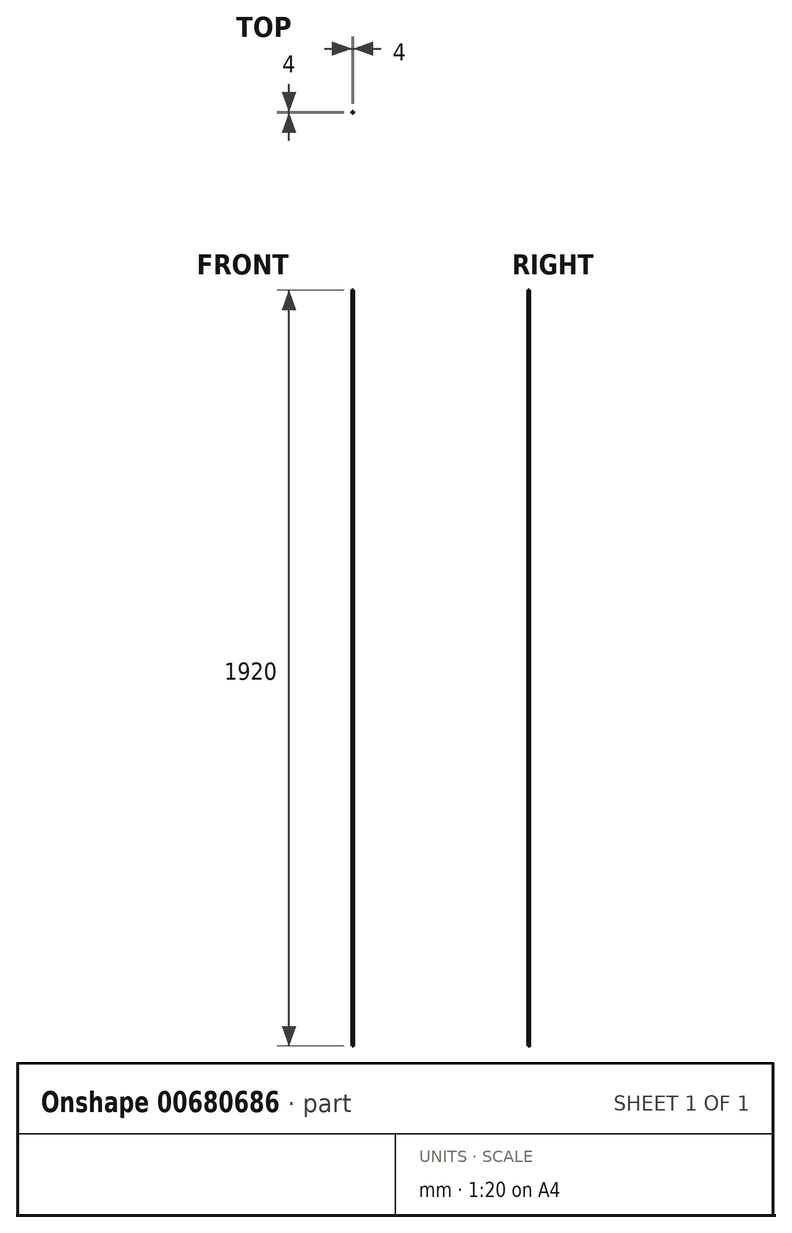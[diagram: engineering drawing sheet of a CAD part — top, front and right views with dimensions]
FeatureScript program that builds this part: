
annotation { "Feature Type Name" : "Feature", "Feature Type Description" : "" }
export const myFeature = defineFeature(function(context is Context, id is Id, definition is map)
    precondition{}
    {
        {
            var Q0;
            Q0=qCreatedBy(makeId("Top.planeOp"),FACE);
            var sketch = newSketch(context, id + "F0", { "sketchPlane" : qUnion([Q0])});
            skCircle(sketch, "E0", {"center": v(0, 0) * mm, "radius": 2 * mm});
            skSolve(sketch);
        }
        {
            var Q0;
            Q0=makeQuery(id+"F0.imprint","IMPRINT",FACE,{"disambiguationData":[TD([[makeQuery(id+"F0.imprint","IMPRINT",EDGE,{"derivedFrom":sQuery(id+"F0.wireOp",EDGE,"E0")}),1.0]])]});
            extrude(context, id + "F1", {"entities" : qUnion([Q0]), "depth" : 1920 * mm, "offsetDistance" : 25 * mm});
        }
    });
